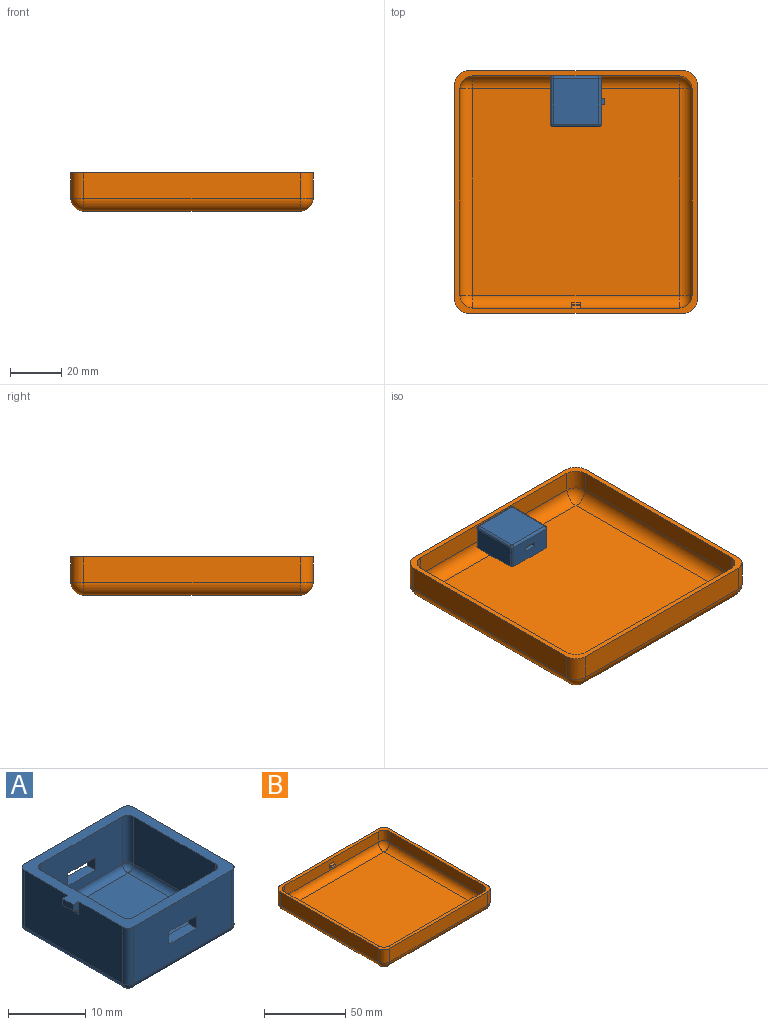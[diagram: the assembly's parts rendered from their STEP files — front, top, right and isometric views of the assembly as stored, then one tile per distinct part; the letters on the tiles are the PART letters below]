
ASSEMBLY  parts=2 mates=1
PART A: 47 faces, bbox 21x20x10 mm
  f0: plane 18x9mm, normal (-1,0,0), area 158mm2, adj f5,f23,f27,f28,f43,f44,f46
  f1: plane 18x9mm, normal (0,-1,0), area 152mm2, adj f5,f28,f32,f34,f39,f40,f41,f42
  f2: plane 18x9mm, normal (0,1,0), area 152mm2, adj f5,f23,f25,f26,f35,f36,f37,f38
  f3: plane 15x7.5mm, normal (0,1,0), area 102.5mm2, adj f5,f11,f15,f16,f39,f40,f41,f42
  f4: plane 15x7.5mm, normal (0,-1,0), area 102.5mm2, adj f5,f13,f19,f22,f35,f36,f37,f38
  f5: plane 21x20mm, normal (0,0,1), area 113mm2, adj f0,f1,f2,f3,f4,f6,f8,f9
  f6: plane 18x9mm, normal (1,0,0), area 162mm2, adj f5,f25,f31,f34
  f7: plane 18x18mm, normal (0,0,-1), area 324mm2, adj f26,f27,f31,f32
  f8: plane 15x7.5mm, normal (-1,0,0), area 112.5mm2, adj f5,f11,f13,f14
  f9: plane 15x7.5mm, normal (1,0,0), area 112.5mm2, adj f5,f16,f20,f22
  f10: plane 15x15mm, normal (0,0,1), area 225mm2, adj f14,f15,f19,f20
  f11: cylinder r=1mm len=7.5mm, axis (0,0,-1), area 11.8mm2, adj f3,f5,f8,f12
  f12: sphere r=1mm, area 1.6mm2, adj f11,f14,f15
  f13: cylinder r=1mm len=7.5mm, axis (0,0,1), area 11.8mm2, adj f4,f5,f8,f17
  f14: cylinder r=1mm len=15mm, axis (0,-1,0), area 23.6mm2, adj f8,f10,f12,f17
  f15: cylinder r=1mm len=15mm, axis (-1,0,0), area 23.6mm2, adj f3,f10,f12,f18
  f16: cylinder r=1mm len=7.5mm, axis (0,0,1), area 11.8mm2, adj f3,f5,f9,f18
  f17: sphere r=1mm, area 1.6mm2, adj f13,f14,f19
  f18: sphere r=1mm, area 1.6mm2, adj f15,f16,f20
  f19: cylinder r=1mm len=15mm, axis (1,0,0), area 23.6mm2, adj f4,f10,f17,f21
  f20: cylinder r=1mm len=15mm, axis (0,1,0), area 23.6mm2, adj f9,f10,f18,f21
  f21: sphere r=1mm, area 1.6mm2, adj f19,f20,f22
  f22: cylinder r=1mm len=7.5mm, axis (0,0,-1), area 11.8mm2, adj f4,f5,f9,f21
  f23: cylinder r=1mm len=9mm, axis (0,0,1), area 14.1mm2, adj f0,f2,f5,f24
  f24: sphere r=1mm, area 1.6mm2, adj f23,f26,f27
  f25: cylinder r=1mm len=9mm, axis (0,0,-1), area 14.1mm2, adj f2,f5,f6,f29
  f26: cylinder r=1mm len=18mm, axis (-1,0,0), area 28.3mm2, adj f2,f7,f24,f29
  f27: cylinder r=1mm len=18mm, axis (0,-1,0), area 28.3mm2, adj f0,f7,f24,f30
  f28: cylinder r=1mm len=9mm, axis (0,0,-1), area 14.1mm2, adj f0,f1,f5,f30
  f29: sphere r=1mm, area 1.6mm2, adj f25,f26,f31
  f30: sphere r=1mm, area 1.6mm2, adj f27,f28,f32
  f31: cylinder r=1mm len=18mm, axis (0,1,0), area 28.3mm2, adj f6,f7,f29,f33
  f32: cylinder r=1mm len=18mm, axis (1,0,0), area 28.3mm2, adj f1,f7,f30,f33
  f33: sphere r=1mm, area 1.6mm2, adj f31,f32,f34
  f34: cylinder r=1mm len=9mm, axis (0,0,1), area 14.1mm2, adj f1,f5,f6,f33
  f35: plane 5x1.5mm, normal (0,0,1), area 7.5mm2, adj f2,f4,f36,f38
  f36: plane 2x1.5mm, normal (1,0,0), area 3mm2, adj f2,f4,f35,f37
  f37: plane 5x1.5mm, normal (0,0,-1), area 7.5mm2, adj f2,f4,f36,f38
  f38: plane 2x1.5mm, normal (-1,0,0), area 3mm2, adj f2,f4,f35,f37
  f39: plane 2x1.5mm, normal (-1,0,0), area 3mm2, adj f1,f3,f40,f42
  f40: plane 5x1.5mm, normal (0,0,-1), area 7.5mm2, adj f1,f3,f39,f41
  f41: plane 2x1.5mm, normal (1,0,0), area 3mm2, adj f1,f3,f40,f42
  f42: plane 5x1.5mm, normal (0,0,1), area 7.5mm2, adj f1,f3,f39,f41
  f43: plane 2x1mm, normal (0,1,0), area 1.2mm2, adj f0,f5,f45,f46
  f44: plane 2x1mm, normal (0,-1,0), area 1.2mm2, adj f0,f5,f45,f46
  f45: plane 2x1mm, normal (-1,0,0), area 2mm2, adj f5,f43,f44,f46
  f46: cylinder r=1mm len=2mm, axis (0,-1,0), area 3.1mm2, adj f0,f43,f44,f45
PART B: 49 faces, bbox 95x95x15 mm
  f0: plane 81x8mm, normal (0,-1,0), area 637.5mm2, adj f2,f13,f19,f22,f39,f41,f43,f44
  f1: plane 81x8mm, normal (0,1,0), area 637.5mm2, adj f2,f11,f15,f16,f35,f37,f45,f46
  f2: plane 95x95mm, normal (0,0,1), area 744mm2, adj f0,f1,f3,f4,f5,f6,f8,f9
  f3: plane 85x10mm, normal (0,-1,0), area 850mm2, adj f2,f28,f32,f34
  f4: plane 85x10mm, normal (1,0,0), area 850mm2, adj f2,f25,f31,f34
  f5: plane 85x10mm, normal (0,1,0), area 850mm2, adj f2,f23,f25,f26
  f6: plane 85x10mm, normal (-1,0,0), area 850mm2, adj f2,f23,f27,f28
  f7: plane 85x85mm, normal (0,0,-1), area 7225mm2, adj f26,f27,f31,f32
  f8: plane 81x8mm, normal (-1,0,0), area 648mm2, adj f2,f11,f13,f14
  f9: plane 81x8mm, normal (1,0,0), area 648mm2, adj f2,f16,f20,f22
  f10: plane 81x81mm, normal (0,0,1), area 6561mm2, adj f14,f15,f19,f20
  f11: cylinder r=5mm len=8mm, axis (0,0,-1), area 62.8mm2, adj f1,f2,f8,f12
  f12: sphere r=5mm, area 39.3mm2, adj f11,f14,f15
  f13: cylinder r=5mm len=8mm, axis (0,0,1), area 62.8mm2, adj f0,f2,f8,f17
  f14: cylinder r=5mm len=81mm, axis (0,-1,0), area 636.2mm2, adj f8,f10,f12,f17
  f15: cylinder r=5mm len=81mm, axis (-1,0,0), area 636.2mm2, adj f1,f10,f12,f18
  f16: cylinder r=5mm len=8mm, axis (0,0,1), area 62.8mm2, adj f1,f2,f9,f18
  f17: sphere r=5mm, area 39.3mm2, adj f13,f14,f19
  f18: sphere r=5mm, area 39.3mm2, adj f15,f16,f20
  f19: cylinder r=5mm len=81mm, axis (1,0,0), area 636.2mm2, adj f0,f10,f17,f21
  f20: cylinder r=5mm len=81mm, axis (0,1,0), area 636.2mm2, adj f9,f10,f18,f21
  f21: sphere r=5mm, area 39.3mm2, adj f19,f20,f22
  f22: cylinder r=5mm len=8mm, axis (0,0,-1), area 62.8mm2, adj f0,f2,f9,f21
  f23: cylinder r=5mm len=10mm, axis (0,0,1), area 78.5mm2, adj f2,f5,f6,f24
  f24: sphere r=5mm, area 39.3mm2, adj f23,f26,f27
  f25: cylinder r=5mm len=10mm, axis (0,0,-1), area 78.5mm2, adj f2,f4,f5,f29
  f26: cylinder r=5mm len=85mm, axis (-1,0,0), area 667.6mm2, adj f5,f7,f24,f29
  f27: cylinder r=5mm len=85mm, axis (0,-1,0), area 667.6mm2, adj f6,f7,f24,f30
  f28: cylinder r=5mm len=10mm, axis (0,0,-1), area 78.5mm2, adj f2,f3,f6,f30
  f29: sphere r=5mm, area 39.3mm2, adj f25,f26,f31
  f30: sphere r=5mm, area 39.3mm2, adj f27,f28,f32
  f31: cylinder r=5mm len=85mm, axis (0,1,0), area 667.6mm2, adj f4,f7,f29,f33
  f32: cylinder r=5mm len=85mm, axis (1,0,0), area 667.6mm2, adj f3,f7,f30,f33
  f33: sphere r=5mm, area 39.3mm2, adj f31,f32,f34
  f34: cylinder r=5mm len=10mm, axis (0,0,1), area 78.5mm2, adj f2,f3,f4,f33
  f35: plane 3x2mm, normal (1,0,0), area 2.3mm2, adj f1,f36,f38,f45,f46,f48
  f36: plane 3.5x0.5mm, normal (0,0,1), area 1.8mm2, adj f35,f37,f45,f48
  f37: plane 3x2mm, normal (-1,0,0), area 2.3mm2, adj f1,f36,f38,f45,f46,f48
  f38: plane 3.5x0.5mm, normal (0,0,-1), area 1.8mm2, adj f35,f37,f46,f48
  f39: plane 3x2mm, normal (1,0,0), area 2.3mm2, adj f0,f40,f42,f43,f44,f47
  f40: plane 3.5x0.5mm, normal (0,0,1), area 1.8mm2, adj f39,f41,f43,f47
  f41: plane 3x2mm, normal (-1,0,0), area 2.3mm2, adj f0,f40,f42,f43,f44,f47
  f42: plane 3.5x0.5mm, normal (0,0,-1), area 1.8mm2, adj f39,f41,f44,f47
  f43: cylinder r=1mm len=3.5mm, axis (1,0,0), area 5.5mm2, adj f0,f39,f40,f41
  f44: cylinder r=1mm len=3.5mm, axis (-1,0,0), area 5.5mm2, adj f0,f39,f41,f42
  f45: cylinder r=1mm len=3.5mm, axis (-1,0,0), area 5.5mm2, adj f1,f35,f36,f37
  f46: cylinder r=1mm len=3.5mm, axis (1,0,0), area 5.5mm2, adj f1,f35,f37,f38
  f47: cylinder r=0.5mm len=3.5mm, axis (1,0,0), area 5.5mm2, adj f39,f40,f41,f42
  f48: cylinder r=0.5mm len=3.5mm, axis (-1,0,0), area 5.5mm2, adj f35,f36,f37,f38
PLACE A rot(axis=(0,1,0),180deg) t=(9.24,55.32,-21.4)mm
PLACE B t=(9.24,19.82,-36.4)mm
MATE fastened A.f2 <-> B.f0  axis (0,1,0) through (9.24,65.32,-26.4)mm
